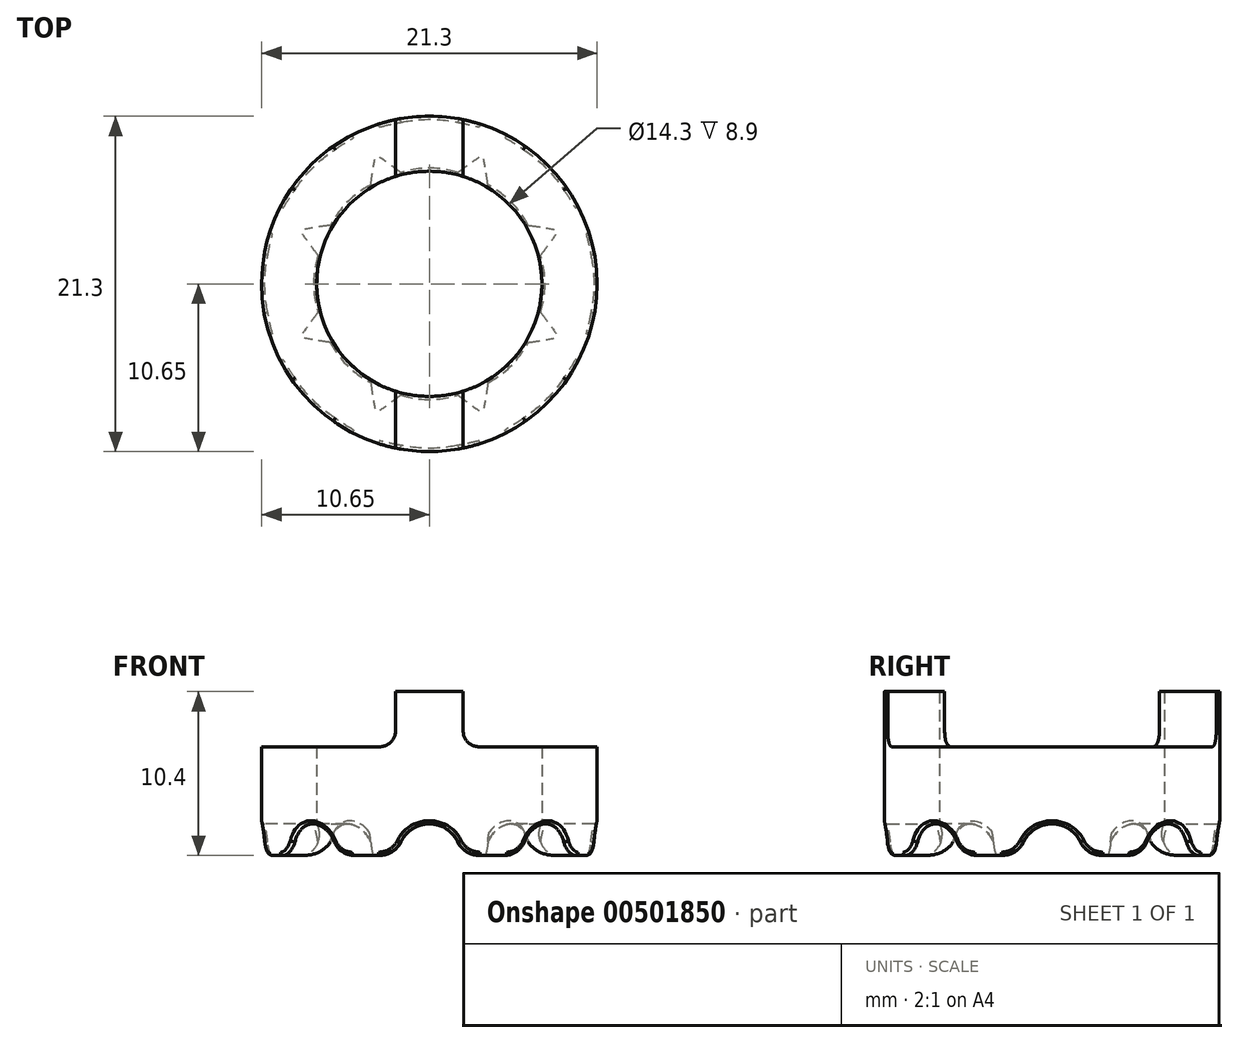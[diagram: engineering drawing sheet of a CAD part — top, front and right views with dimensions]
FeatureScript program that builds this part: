
annotation { "Feature Type Name" : "Feature", "Feature Type Description" : "" }
export const myFeature = defineFeature(function(context is Context, id is Id, definition is map)
    precondition{}
    {
        {
            var Q0;
            Q0=qCreatedBy(makeId("Top.planeOp"),FACE);
            var sketch = newSketch(context, id + "F0", { "sketchPlane" : qUnion([Q0])});
            skCircle(sketch, "E0", {"center": v(0, 0) * mm, "radius": 7.15 * mm});
            skCircle(sketch, "E1", {"center": v(0, 0) * mm, "radius": 10.65 * mm});
            skSolve(sketch);
        }
        {
            var Q0;
            Q0 = qSketchRegion(id + "F0", true);
            extrude(context, id + "F1", {"entities" : qUnion([Q0]), "depth" : 10.4 * mm});
        }
        {
            var Q0;
            Q0=qCreatedBy(makeId("Front.planeOp"),FACE);
            var sketch = newSketch(context, id + "F2", { "sketchPlane" : qUnion([Q0])});
            skLineSegment(sketch, "E2.0", {"start": v(-10.65, 10.4) * mm, "end": v(-2.15, 10.4) * mm});
            skLineSegment(sketch, "E3.0", {"start": v(-10.65, 6.9) * mm, "end": v(-3.15, 6.9) * mm});
            skLineSegment(sketch, "E4.0", {"start": v(-2.15, 10.4) * mm, "end": v(-2.15, 7.9) * mm});
            skLineSegment(sketch, "E5.0", {"start": v(2.15, 10.4) * mm, "end": v(2.15, 7.9) * mm});
            skLineSegment(sketch, "E6", {"start": v(-10.65, 10.4) * mm, "end": v(-10.65, 6.9) * mm});
            skLineSegment(sketch, "E7", {"start": v(10.65, 10.4) * mm, "end": v(10.65, 6.9) * mm});
            skLineSegment(sketch, "E8.trimOffspring", {"start": v(3.15, 6.9) * mm, "end": v(10.65, 6.9) * mm});
            skLineSegment(sketch, "E9.trimOffspring", {"start": v(2.15, 10.4) * mm, "end": v(10.65, 10.4) * mm});
            skPoint(sketch, "E10.visualSharp", {"position": v(-2.15, 6.9) * mm});
            skArc(sketch, "E10.filletArc", {"start": v(-3.15, 6.9) * mm, "mid": v(-2.44, 7.2) * mm, "end": v(-2.15, 7.9) * mm});
            skPoint(sketch, "E11.visualSharp", {"position": v(2.15, 6.9) * mm});
            skArc(sketch, "E11.filletArc", {"start": v(2.15, 7.9) * mm, "mid": v(2.44, 7.2) * mm, "end": v(3.15, 6.9) * mm});
            skSolve(sketch);
        }
        {
            var Q0;
            Q0 = qSketchRegion(id + "F2", true);
            extrude(context, id + "F3", {"entities" : qUnion([Q0]), "operationType" : NewBodyOperationType.REMOVE, "endBound" : BoundingType.THROUGH_ALL, "oppositeDirection" : true, "depth" : 25 * mm, "hasSecondDirection" : true, "secondDirectionBound" : SecondDirectionBoundingType.THROUGH_ALL, "secondDirectionOppositeDirection" : false, "secondDirectionDepth" : 25 * mm});
        }
        {
            var Q0;
            Q0=qCreatedBy(makeId("Front.planeOp"),FACE);
            var sketch = newSketch(context, id + "F4", { "sketchPlane" : qUnion([Q0])});
            skCircle(sketch, "E12", {"center": v(0, 0) * mm, "radius": 2 * mm});
            skSolve(sketch);
        }
        {
            var Q0;
            Q0 = qSketchRegion(id + "F4", true);
            extrude(context, id + "F5", {"entities" : qUnion([Q0]), "operationType" : NewBodyOperationType.REMOVE, "endBound" : BoundingType.THROUGH_ALL, "depth" : 25 * mm, "hasSecondDirection" : true, "secondDirectionBound" : SecondDirectionBoundingType.THROUGH_ALL, "secondDirectionOppositeDirection" : true, "secondDirectionDepth" : 25 * mm});
        }
        {
            var Q0;
            Q0=qCreatedBy(makeId("Right.planeOp"),FACE);
            var sketch = newSketch(context, id + "F6", { "sketchPlane" : qUnion([Q0])});
            skCircle(sketch, "E13", {"center": v(0, 0) * mm, "radius": 2 * mm});
            skSolve(sketch);
        }
        {
            var Q0;
            Q0 = qSketchRegion(id + "F6", true);
            extrude(context, id + "F7", {"entities" : qUnion([Q0]), "operationType" : NewBodyOperationType.REMOVE, "endBound" : BoundingType.THROUGH_ALL, "depth" : 25 * mm, "hasSecondDirection" : true, "secondDirectionBound" : SecondDirectionBoundingType.THROUGH_ALL, "secondDirectionOppositeDirection" : true, "secondDirectionDepth" : 25 * mm});
        }
        {
            var Q0;
            Q0=qCreatedBy(makeId("Front.planeOp"),FACE);
            var sketch = newSketch(context, id + "F8", { "sketchPlane" : qUnion([Q0])});
            skLineSegment(sketch, "E14", {"start": v(0, 0) * mm, "end": v(0, -32.86) * mm});
            skLineSegment(sketch, "E15", {"start": v(0, 0) * mm, "end": v(12.09, 0) * mm});
            skSolve(sketch);
        }
        {
            var Q0;
            Q0=sQuery(id+"F8.wireOp",EDGE,"E14");
            cPlane(context, id + "F9", {"entities" : qUnion([Q0]), "cplaneType" : CPlaneType.LINE_ANGLE, "offset" : 25 * mm, "angle" : 45 * degree, "width" : 150 * mm, "height" : 150 * mm});
        }
        {
            var Q0;
            Q0=sQuery(id+"F8.wireOp",EDGE,"E14");
            cPlane(context, id + "F10", {"entities" : qUnion([Q0]), "cplaneType" : CPlaneType.LINE_ANGLE, "offset" : 25 * mm, "angle" : 135 * degree, "width" : 150 * mm, "height" : 150 * mm});
        }
        {
            var Q0;
            Q0=qCreatedBy(id+"F10.planeOp",FACE);
            var sketch = newSketch(context, id + "F11", { "sketchPlane" : qUnion([Q0])});
            skCircle(sketch, "E16", {"center": v(0, 0) * mm, "radius": 2 * mm});
            skSolve(sketch);
        }
        {
            var Q0;
            Q0 = qSketchRegion(id + "F11", true);
            extrude(context, id + "F12", {"entities" : qUnion([Q0]), "operationType" : NewBodyOperationType.REMOVE, "endBound" : BoundingType.THROUGH_ALL, "depth" : 25 * mm, "hasSecondDirection" : true, "secondDirectionBound" : SecondDirectionBoundingType.THROUGH_ALL, "secondDirectionOppositeDirection" : true, "secondDirectionDepth" : 25 * mm});
        }
        {
            var Q0;
            Q0=qCreatedBy(id+"F9.planeOp",FACE);
            var sketch = newSketch(context, id + "F13", { "sketchPlane" : qUnion([Q0])});
            skCircle(sketch, "E17", {"center": v(0, 0) * mm, "radius": 2 * mm});
            skSolve(sketch);
        }
        {
            var Q0;
            Q0 = qSketchRegion(id + "F13", true);
            extrude(context, id + "F14", {"entities" : qUnion([Q0]), "operationType" : NewBodyOperationType.REMOVE, "endBound" : BoundingType.THROUGH_ALL, "depth" : 25 * mm, "hasSecondDirection" : true, "secondDirectionBound" : SecondDirectionBoundingType.THROUGH_ALL, "secondDirectionOppositeDirection" : true, "secondDirectionDepth" : 25 * mm});
        }
        {
            var Q0;
            {var subQ0=sQuery(id+"F0.wireOp",EDGE,"E0");var subQ1=sQuery(id+"F0.wireOp",EDGE,"E1");Q0=makeQuery(id+"F14.boolean.opBoolean","INTERSECT",EDGE,{"disambiguationData":[OD(1.0)],"derivedFrom":[makeQuery(id+"F7.boolean.opBoolean","SPLIT",FACE,{"disambiguationData":[TD([makeQuery(id+"F5.boolean.opBoolean","COPY",FACE,{"disambiguationData":[OD(0.0)],"derivedFrom":makeQuery(id+"F5.opExtrude","SWEPT_FACE",FACE,{"disambiguationData":[OSD([sQuery(id+"F4.wireOp",EDGE,"E12")])]})})])],"derivedFrom":makeQuery(id+"F5.boolean.opBoolean","SPLIT",FACE,{"disambiguationData":[OD(1.0)],"derivedFrom":makeQuery(id+"F1.opExtrude","CAP_FACE",FACE,{"disambiguationData":[OSD([subQ0,subQ1])],"isStart":true})})}),makeQuery(id+"F14.opExtrude","SWEPT_FACE",FACE,{"disambiguationData":[OSD([sQuery(id+"F13.wireOp",EDGE,"E17")])]})]});}
            var Q1;
            Q1=makeQuery(id+"F7.boolean.opBoolean","INTERSECT",EDGE,{"disambiguationData":[OD(0.0)],"derivedFrom":[makeQuery(id+"F5.boolean.opBoolean","SPLIT",FACE,{"disambiguationData":[OD(1.0)],"derivedFrom":makeQuery(id+"F1.opExtrude","CAP_FACE",FACE,{"disambiguationData":[OSD([sQuery(id+"F0.wireOp",EDGE,"E0"),sQuery(id+"F0.wireOp",EDGE,"E1")])],"isStart":true})}),makeQuery(id+"F7.opExtrude","SWEPT_FACE",FACE,{"disambiguationData":[OSD([sQuery(id+"F6.wireOp",EDGE,"E13")])]})]});
            var Q2;
            {var subQ0=sQuery(id+"F0.wireOp",EDGE,"E0");var subQ3=makeQuery(id+"F7.opExtrude","SWEPT_FACE",FACE,{"disambiguationData":[OSD([sQuery(id+"F6.wireOp",EDGE,"E13")])]});Q2=makeQuery(id+"F14.boolean.opBoolean","SPLIT",EDGE,{"disambiguationData":[TD([makeQuery(id+"F7.boolean.opBoolean","COPY",FACE,{"disambiguationData":[OD(1.0)],"derivedFrom":subQ3})])],"derivedFrom":makeQuery(id+"F7.boolean.opBoolean","SPLIT",EDGE,{"disambiguationData":[TD([makeQuery(id+"F5.boolean.opBoolean","COPY",FACE,{"disambiguationData":[OD(0.0)],"derivedFrom":makeQuery(id+"F5.opExtrude","SWEPT_FACE",FACE,{"disambiguationData":[OSD([sQuery(id+"F4.wireOp",EDGE,"E12")])]})})])],"derivedFrom":makeQuery(id+"F5.boolean.opBoolean","SPLIT",EDGE,{"disambiguationData":[OD(1.0)],"derivedFrom":makeQuery(id+"F1.opExtrude","CAP_EDGE",EDGE,{"disambiguationData":[OSD([subQ0])],"isStart":true})})})});}
            var Q3;
            {var subQ0=sQuery(id+"F0.wireOp",EDGE,"E0");var subQ3=makeQuery(id+"F5.boolean.opBoolean","COPY",FACE,{"disambiguationData":[OD(0.0)],"derivedFrom":makeQuery(id+"F5.opExtrude","SWEPT_FACE",FACE,{"disambiguationData":[OSD([sQuery(id+"F4.wireOp",EDGE,"E12")])]})});Q3=makeQuery(id+"F14.boolean.opBoolean","SPLIT",EDGE,{"disambiguationData":[TD([subQ3])],"derivedFrom":makeQuery(id+"F7.boolean.opBoolean","SPLIT",EDGE,{"disambiguationData":[TD([subQ3])],"derivedFrom":makeQuery(id+"F5.boolean.opBoolean","SPLIT",EDGE,{"disambiguationData":[OD(1.0)],"derivedFrom":makeQuery(id+"F1.opExtrude","CAP_EDGE",EDGE,{"disambiguationData":[OSD([subQ0])],"isStart":true})})})});}
            var Q4;
            {var subQ0=sQuery(id+"F0.wireOp",EDGE,"E0");var subQ3=makeQuery(id+"F5.boolean.opBoolean","COPY",FACE,{"disambiguationData":[OD(0.0)],"derivedFrom":makeQuery(id+"F5.opExtrude","SWEPT_FACE",FACE,{"disambiguationData":[OSD([sQuery(id+"F4.wireOp",EDGE,"E12")])]})});Q4=makeQuery(id+"F12.boolean.opBoolean","SPLIT",EDGE,{"disambiguationData":[TD([subQ3])],"derivedFrom":makeQuery(id+"F7.boolean.opBoolean","SPLIT",EDGE,{"disambiguationData":[TD([subQ3])],"derivedFrom":makeQuery(id+"F5.boolean.opBoolean","SPLIT",EDGE,{"disambiguationData":[OD(0.0)],"derivedFrom":makeQuery(id+"F1.opExtrude","CAP_EDGE",EDGE,{"disambiguationData":[OSD([subQ0])],"isStart":true})})})});}
            var Q5;
            {var subQ0=sQuery(id+"F0.wireOp",EDGE,"E0");var subQ3=makeQuery(id+"F7.opExtrude","SWEPT_FACE",FACE,{"disambiguationData":[OSD([sQuery(id+"F6.wireOp",EDGE,"E13")])]});Q5=makeQuery(id+"F12.boolean.opBoolean","SPLIT",EDGE,{"disambiguationData":[TD([makeQuery(id+"F7.boolean.opBoolean","COPY",FACE,{"disambiguationData":[OD(0.0)],"derivedFrom":subQ3})])],"derivedFrom":makeQuery(id+"F7.boolean.opBoolean","SPLIT",EDGE,{"disambiguationData":[TD([makeQuery(id+"F5.boolean.opBoolean","COPY",FACE,{"disambiguationData":[OD(0.0)],"derivedFrom":makeQuery(id+"F5.opExtrude","SWEPT_FACE",FACE,{"disambiguationData":[OSD([sQuery(id+"F4.wireOp",EDGE,"E12")])]})})])],"derivedFrom":makeQuery(id+"F5.boolean.opBoolean","SPLIT",EDGE,{"disambiguationData":[OD(0.0)],"derivedFrom":makeQuery(id+"F1.opExtrude","CAP_EDGE",EDGE,{"disambiguationData":[OSD([subQ0])],"isStart":true})})})});}
            var Q6;
            {var subQ0=sQuery(id+"F0.wireOp",EDGE,"E0");var subQ3=makeQuery(id+"F7.opExtrude","SWEPT_FACE",FACE,{"disambiguationData":[OSD([sQuery(id+"F6.wireOp",EDGE,"E13")])]});Q6=makeQuery(id+"F14.boolean.opBoolean","SPLIT",EDGE,{"disambiguationData":[TD([makeQuery(id+"F7.boolean.opBoolean","COPY",FACE,{"disambiguationData":[OD(0.0)],"derivedFrom":subQ3})])],"derivedFrom":makeQuery(id+"F7.boolean.opBoolean","SPLIT",EDGE,{"disambiguationData":[TD([makeQuery(id+"F5.boolean.opBoolean","COPY",FACE,{"disambiguationData":[OD(1.0)],"derivedFrom":makeQuery(id+"F5.opExtrude","SWEPT_FACE",FACE,{"disambiguationData":[OSD([sQuery(id+"F4.wireOp",EDGE,"E12")])]})})])],"derivedFrom":makeQuery(id+"F5.boolean.opBoolean","SPLIT",EDGE,{"disambiguationData":[OD(0.0)],"derivedFrom":makeQuery(id+"F1.opExtrude","CAP_EDGE",EDGE,{"disambiguationData":[OSD([subQ0])],"isStart":true})})})});}
            var Q7;
            {var subQ0=sQuery(id+"F0.wireOp",EDGE,"E0");var subQ3=makeQuery(id+"F5.boolean.opBoolean","COPY",FACE,{"disambiguationData":[OD(1.0)],"derivedFrom":makeQuery(id+"F5.opExtrude","SWEPT_FACE",FACE,{"disambiguationData":[OSD([sQuery(id+"F4.wireOp",EDGE,"E12")])]})});Q7=makeQuery(id+"F14.boolean.opBoolean","SPLIT",EDGE,{"disambiguationData":[TD([subQ3])],"derivedFrom":makeQuery(id+"F7.boolean.opBoolean","SPLIT",EDGE,{"disambiguationData":[TD([subQ3])],"derivedFrom":makeQuery(id+"F5.boolean.opBoolean","SPLIT",EDGE,{"disambiguationData":[OD(0.0)],"derivedFrom":makeQuery(id+"F1.opExtrude","CAP_EDGE",EDGE,{"disambiguationData":[OSD([subQ0])],"isStart":true})})})});}
            var Q8;
            {var subQ0=sQuery(id+"F0.wireOp",EDGE,"E0");var subQ3=makeQuery(id+"F5.boolean.opBoolean","COPY",FACE,{"disambiguationData":[OD(1.0)],"derivedFrom":makeQuery(id+"F5.opExtrude","SWEPT_FACE",FACE,{"disambiguationData":[OSD([sQuery(id+"F4.wireOp",EDGE,"E12")])]})});Q8=makeQuery(id+"F12.boolean.opBoolean","SPLIT",EDGE,{"disambiguationData":[TD([subQ3])],"derivedFrom":makeQuery(id+"F7.boolean.opBoolean","SPLIT",EDGE,{"disambiguationData":[TD([subQ3])],"derivedFrom":makeQuery(id+"F5.boolean.opBoolean","SPLIT",EDGE,{"disambiguationData":[OD(1.0)],"derivedFrom":makeQuery(id+"F1.opExtrude","CAP_EDGE",EDGE,{"disambiguationData":[OSD([subQ0])],"isStart":true})})})});}
            var Q9;
            {var subQ0=sQuery(id+"F0.wireOp",EDGE,"E0");var subQ3=makeQuery(id+"F7.opExtrude","SWEPT_FACE",FACE,{"disambiguationData":[OSD([sQuery(id+"F6.wireOp",EDGE,"E13")])]});Q9=makeQuery(id+"F12.boolean.opBoolean","SPLIT",EDGE,{"disambiguationData":[TD([makeQuery(id+"F7.boolean.opBoolean","COPY",FACE,{"disambiguationData":[OD(1.0)],"derivedFrom":subQ3})])],"derivedFrom":makeQuery(id+"F7.boolean.opBoolean","SPLIT",EDGE,{"disambiguationData":[TD([makeQuery(id+"F5.boolean.opBoolean","COPY",FACE,{"disambiguationData":[OD(1.0)],"derivedFrom":makeQuery(id+"F5.opExtrude","SWEPT_FACE",FACE,{"disambiguationData":[OSD([sQuery(id+"F4.wireOp",EDGE,"E12")])]})})])],"derivedFrom":makeQuery(id+"F5.boolean.opBoolean","SPLIT",EDGE,{"disambiguationData":[OD(1.0)],"derivedFrom":makeQuery(id+"F1.opExtrude","CAP_EDGE",EDGE,{"disambiguationData":[OSD([subQ0])],"isStart":true})})})});}
            var Q10;
            Q10=makeQuery(id+"F7.boolean.opBoolean","INTERSECT",EDGE,{"disambiguationData":[OD(1.0)],"derivedFrom":[makeQuery(id+"F5.boolean.opBoolean","SPLIT",FACE,{"disambiguationData":[OD(1.0)],"derivedFrom":makeQuery(id+"F1.opExtrude","CAP_FACE",FACE,{"disambiguationData":[OSD([sQuery(id+"F0.wireOp",EDGE,"E0"),sQuery(id+"F0.wireOp",EDGE,"E1")])],"isStart":true})}),makeQuery(id+"F7.opExtrude","SWEPT_FACE",FACE,{"disambiguationData":[OSD([sQuery(id+"F6.wireOp",EDGE,"E13")])]})]});
            var Q11;
            {var subQ0=sQuery(id+"F0.wireOp",EDGE,"E0");var subQ1=sQuery(id+"F0.wireOp",EDGE,"E1");Q11=makeQuery(id+"F12.boolean.opBoolean","INTERSECT",EDGE,{"disambiguationData":[OD(1.0)],"derivedFrom":[makeQuery(id+"F7.boolean.opBoolean","SPLIT",FACE,{"disambiguationData":[TD([makeQuery(id+"F5.boolean.opBoolean","COPY",FACE,{"disambiguationData":[OD(1.0)],"derivedFrom":makeQuery(id+"F5.opExtrude","SWEPT_FACE",FACE,{"disambiguationData":[OSD([sQuery(id+"F4.wireOp",EDGE,"E12")])]})})])],"derivedFrom":makeQuery(id+"F5.boolean.opBoolean","SPLIT",FACE,{"disambiguationData":[OD(1.0)],"derivedFrom":makeQuery(id+"F1.opExtrude","CAP_FACE",FACE,{"disambiguationData":[OSD([subQ0,subQ1])],"isStart":true})})}),makeQuery(id+"F12.opExtrude","SWEPT_FACE",FACE,{"disambiguationData":[OSD([sQuery(id+"F11.wireOp",EDGE,"E16")])]})]});}
            var Q12;
            {var subQ0=sQuery(id+"F0.wireOp",EDGE,"E0");var subQ1=sQuery(id+"F0.wireOp",EDGE,"E1");Q12=makeQuery(id+"F12.boolean.opBoolean","INTERSECT",EDGE,{"disambiguationData":[OD(0.0)],"derivedFrom":[makeQuery(id+"F7.boolean.opBoolean","SPLIT",FACE,{"disambiguationData":[TD([makeQuery(id+"F5.boolean.opBoolean","COPY",FACE,{"disambiguationData":[OD(1.0)],"derivedFrom":makeQuery(id+"F5.opExtrude","SWEPT_FACE",FACE,{"disambiguationData":[OSD([sQuery(id+"F4.wireOp",EDGE,"E12")])]})})])],"derivedFrom":makeQuery(id+"F5.boolean.opBoolean","SPLIT",FACE,{"disambiguationData":[OD(1.0)],"derivedFrom":makeQuery(id+"F1.opExtrude","CAP_FACE",FACE,{"disambiguationData":[OSD([subQ0,subQ1])],"isStart":true})})}),makeQuery(id+"F12.opExtrude","SWEPT_FACE",FACE,{"disambiguationData":[OSD([sQuery(id+"F11.wireOp",EDGE,"E16")])]})]});}
            var Q13;
            Q13=makeQuery(id+"F5.boolean.opBoolean","INTERSECT",EDGE,{"disambiguationData":[OD(3.0)],"derivedFrom":[makeQuery(id+"F1.opExtrude","CAP_FACE",FACE,{"disambiguationData":[OSD([sQuery(id+"F0.wireOp",EDGE,"E0"),sQuery(id+"F0.wireOp",EDGE,"E1")])],"isStart":true}),makeQuery(id+"F5.opExtrude","SWEPT_FACE",FACE,{"disambiguationData":[OSD([sQuery(id+"F4.wireOp",EDGE,"E12")])]})]});
            var Q14;
            Q14=makeQuery(id+"F5.boolean.opBoolean","INTERSECT",EDGE,{"disambiguationData":[OD(2.0)],"derivedFrom":[makeQuery(id+"F1.opExtrude","CAP_FACE",FACE,{"disambiguationData":[OSD([sQuery(id+"F0.wireOp",EDGE,"E0"),sQuery(id+"F0.wireOp",EDGE,"E1")])],"isStart":true}),makeQuery(id+"F5.opExtrude","SWEPT_FACE",FACE,{"disambiguationData":[OSD([sQuery(id+"F4.wireOp",EDGE,"E12")])]})]});
            var Q15;
            {var subQ0=sQuery(id+"F0.wireOp",EDGE,"E0");var subQ1=sQuery(id+"F0.wireOp",EDGE,"E1");Q15=makeQuery(id+"F14.boolean.opBoolean","INTERSECT",EDGE,{"disambiguationData":[OD(0.0)],"derivedFrom":[makeQuery(id+"F7.boolean.opBoolean","SPLIT",FACE,{"disambiguationData":[TD([makeQuery(id+"F5.boolean.opBoolean","COPY",FACE,{"disambiguationData":[OD(1.0)],"derivedFrom":makeQuery(id+"F5.opExtrude","SWEPT_FACE",FACE,{"disambiguationData":[OSD([sQuery(id+"F4.wireOp",EDGE,"E12")])]})})])],"derivedFrom":makeQuery(id+"F5.boolean.opBoolean","SPLIT",FACE,{"disambiguationData":[OD(0.0)],"derivedFrom":makeQuery(id+"F1.opExtrude","CAP_FACE",FACE,{"disambiguationData":[OSD([subQ0,subQ1])],"isStart":true})})}),makeQuery(id+"F14.opExtrude","SWEPT_FACE",FACE,{"disambiguationData":[OSD([sQuery(id+"F13.wireOp",EDGE,"E17")])]})]});}
            var Q16;
            {var subQ0=sQuery(id+"F0.wireOp",EDGE,"E0");var subQ1=sQuery(id+"F0.wireOp",EDGE,"E1");Q16=makeQuery(id+"F14.boolean.opBoolean","INTERSECT",EDGE,{"disambiguationData":[OD(1.0)],"derivedFrom":[makeQuery(id+"F7.boolean.opBoolean","SPLIT",FACE,{"disambiguationData":[TD([makeQuery(id+"F5.boolean.opBoolean","COPY",FACE,{"disambiguationData":[OD(1.0)],"derivedFrom":makeQuery(id+"F5.opExtrude","SWEPT_FACE",FACE,{"disambiguationData":[OSD([sQuery(id+"F4.wireOp",EDGE,"E12")])]})})])],"derivedFrom":makeQuery(id+"F5.boolean.opBoolean","SPLIT",FACE,{"disambiguationData":[OD(0.0)],"derivedFrom":makeQuery(id+"F1.opExtrude","CAP_FACE",FACE,{"disambiguationData":[OSD([subQ0,subQ1])],"isStart":true})})}),makeQuery(id+"F14.opExtrude","SWEPT_FACE",FACE,{"disambiguationData":[OSD([sQuery(id+"F13.wireOp",EDGE,"E17")])]})]});}
            var Q17;
            Q17=makeQuery(id+"F7.boolean.opBoolean","INTERSECT",EDGE,{"disambiguationData":[OD(1.0)],"derivedFrom":[makeQuery(id+"F5.boolean.opBoolean","SPLIT",FACE,{"disambiguationData":[OD(0.0)],"derivedFrom":makeQuery(id+"F1.opExtrude","CAP_FACE",FACE,{"disambiguationData":[OSD([sQuery(id+"F0.wireOp",EDGE,"E0"),sQuery(id+"F0.wireOp",EDGE,"E1")])],"isStart":true})}),makeQuery(id+"F7.opExtrude","SWEPT_FACE",FACE,{"disambiguationData":[OSD([sQuery(id+"F6.wireOp",EDGE,"E13")])]})]});
            var Q18;
            Q18=makeQuery(id+"F7.boolean.opBoolean","INTERSECT",EDGE,{"disambiguationData":[OD(0.0)],"derivedFrom":[makeQuery(id+"F5.boolean.opBoolean","SPLIT",FACE,{"disambiguationData":[OD(0.0)],"derivedFrom":makeQuery(id+"F1.opExtrude","CAP_FACE",FACE,{"disambiguationData":[OSD([sQuery(id+"F0.wireOp",EDGE,"E0"),sQuery(id+"F0.wireOp",EDGE,"E1")])],"isStart":true})}),makeQuery(id+"F7.opExtrude","SWEPT_FACE",FACE,{"disambiguationData":[OSD([sQuery(id+"F6.wireOp",EDGE,"E13")])]})]});
            var Q19;
            {var subQ0=sQuery(id+"F0.wireOp",EDGE,"E0");var subQ1=sQuery(id+"F0.wireOp",EDGE,"E1");Q19=makeQuery(id+"F12.boolean.opBoolean","INTERSECT",EDGE,{"disambiguationData":[OD(1.0)],"derivedFrom":[makeQuery(id+"F7.boolean.opBoolean","SPLIT",FACE,{"disambiguationData":[TD([makeQuery(id+"F5.boolean.opBoolean","COPY",FACE,{"disambiguationData":[OD(0.0)],"derivedFrom":makeQuery(id+"F5.opExtrude","SWEPT_FACE",FACE,{"disambiguationData":[OSD([sQuery(id+"F4.wireOp",EDGE,"E12")])]})})])],"derivedFrom":makeQuery(id+"F5.boolean.opBoolean","SPLIT",FACE,{"disambiguationData":[OD(0.0)],"derivedFrom":makeQuery(id+"F1.opExtrude","CAP_FACE",FACE,{"disambiguationData":[OSD([subQ0,subQ1])],"isStart":true})})}),makeQuery(id+"F12.opExtrude","SWEPT_FACE",FACE,{"disambiguationData":[OSD([sQuery(id+"F11.wireOp",EDGE,"E16")])]})]});}
            var Q20;
            {var subQ0=sQuery(id+"F0.wireOp",EDGE,"E0");var subQ1=sQuery(id+"F0.wireOp",EDGE,"E1");Q20=makeQuery(id+"F12.boolean.opBoolean","INTERSECT",EDGE,{"disambiguationData":[OD(0.0)],"derivedFrom":[makeQuery(id+"F7.boolean.opBoolean","SPLIT",FACE,{"disambiguationData":[TD([makeQuery(id+"F5.boolean.opBoolean","COPY",FACE,{"disambiguationData":[OD(0.0)],"derivedFrom":makeQuery(id+"F5.opExtrude","SWEPT_FACE",FACE,{"disambiguationData":[OSD([sQuery(id+"F4.wireOp",EDGE,"E12")])]})})])],"derivedFrom":makeQuery(id+"F5.boolean.opBoolean","SPLIT",FACE,{"disambiguationData":[OD(0.0)],"derivedFrom":makeQuery(id+"F1.opExtrude","CAP_FACE",FACE,{"disambiguationData":[OSD([subQ0,subQ1])],"isStart":true})})}),makeQuery(id+"F12.opExtrude","SWEPT_FACE",FACE,{"disambiguationData":[OSD([sQuery(id+"F11.wireOp",EDGE,"E16")])]})]});}
            var Q21;
            Q21=makeQuery(id+"F5.boolean.opBoolean","INTERSECT",EDGE,{"disambiguationData":[OD(0.0)],"derivedFrom":[makeQuery(id+"F1.opExtrude","CAP_FACE",FACE,{"disambiguationData":[OSD([sQuery(id+"F0.wireOp",EDGE,"E0"),sQuery(id+"F0.wireOp",EDGE,"E1")])],"isStart":true}),makeQuery(id+"F5.opExtrude","SWEPT_FACE",FACE,{"disambiguationData":[OSD([sQuery(id+"F4.wireOp",EDGE,"E12")])]})]});
            var Q22;
            Q22=makeQuery(id+"F5.boolean.opBoolean","INTERSECT",EDGE,{"disambiguationData":[OD(1.0)],"derivedFrom":[makeQuery(id+"F1.opExtrude","CAP_FACE",FACE,{"disambiguationData":[OSD([sQuery(id+"F0.wireOp",EDGE,"E0"),sQuery(id+"F0.wireOp",EDGE,"E1")])],"isStart":true}),makeQuery(id+"F5.opExtrude","SWEPT_FACE",FACE,{"disambiguationData":[OSD([sQuery(id+"F4.wireOp",EDGE,"E12")])]})]});
            var Q23;
            {var subQ0=sQuery(id+"F0.wireOp",EDGE,"E0");var subQ1=sQuery(id+"F0.wireOp",EDGE,"E1");Q23=makeQuery(id+"F14.boolean.opBoolean","INTERSECT",EDGE,{"disambiguationData":[OD(0.0)],"derivedFrom":[makeQuery(id+"F7.boolean.opBoolean","SPLIT",FACE,{"disambiguationData":[TD([makeQuery(id+"F5.boolean.opBoolean","COPY",FACE,{"disambiguationData":[OD(0.0)],"derivedFrom":makeQuery(id+"F5.opExtrude","SWEPT_FACE",FACE,{"disambiguationData":[OSD([sQuery(id+"F4.wireOp",EDGE,"E12")])]})})])],"derivedFrom":makeQuery(id+"F5.boolean.opBoolean","SPLIT",FACE,{"disambiguationData":[OD(1.0)],"derivedFrom":makeQuery(id+"F1.opExtrude","CAP_FACE",FACE,{"disambiguationData":[OSD([subQ0,subQ1])],"isStart":true})})}),makeQuery(id+"F14.opExtrude","SWEPT_FACE",FACE,{"disambiguationData":[OSD([sQuery(id+"F13.wireOp",EDGE,"E17")])]})]});}
            fillet(context, id + "F15", {"entities" : qUnion([Q0, Q1, Q2, Q3, Q4, Q5, Q6, Q7, Q8, Q9, Q10, Q11, Q12, Q13, Q14, Q15, Q16, Q17, Q18, Q19, Q20, Q21, Q22, Q23]), "radius" : 1.5 * mm, "tangentPropagation" : true, "allowEdgeOverflow" : false});
        }
        {
            var Q0;
            Q0=makeQuery(id+"F5.boolean.opBoolean","INTERSECT",EDGE,{"disambiguationData":[OD(1.0)],"derivedFrom":[makeQuery(id+"F1.opExtrude","SWEPT_FACE",FACE,{"disambiguationData":[OSD([sQuery(id+"F0.wireOp",EDGE,"E1")])]}),makeQuery(id+"F5.opExtrude","SWEPT_FACE",FACE,{"disambiguationData":[OSD([sQuery(id+"F4.wireOp",EDGE,"E12")])]})]});
            fillet(context, id + "F16", {"entities" : qUnion([Q0]), "radius" : 0.2 * mm, "tangentPropagation" : true, "allowEdgeOverflow" : false});
        }
        {
            var Q0;
            Q0=makeQuery(id+"F12.boolean.opBoolean","INTERSECT",EDGE,{"disambiguationData":[OD(0.0)],"derivedFrom":[makeQuery(id+"F1.opExtrude","SWEPT_FACE",FACE,{"disambiguationData":[OSD([sQuery(id+"F0.wireOp",EDGE,"E0")])]}),makeQuery(id+"F12.opExtrude","SWEPT_FACE",FACE,{"disambiguationData":[OSD([sQuery(id+"F11.wireOp",EDGE,"E16")])]})]});
            var Q1;
            Q1=makeQuery(id+"F5.boolean.opBoolean","INTERSECT",EDGE,{"disambiguationData":[OD(0.0)],"derivedFrom":[makeQuery(id+"F1.opExtrude","SWEPT_FACE",FACE,{"disambiguationData":[OSD([sQuery(id+"F0.wireOp",EDGE,"E0")])]}),makeQuery(id+"F5.opExtrude","SWEPT_FACE",FACE,{"disambiguationData":[OSD([sQuery(id+"F4.wireOp",EDGE,"E12")])]})]});
            var Q2;
            Q2=makeQuery(id+"F14.boolean.opBoolean","INTERSECT",EDGE,{"disambiguationData":[OD(1.0)],"derivedFrom":[makeQuery(id+"F1.opExtrude","SWEPT_FACE",FACE,{"disambiguationData":[OSD([sQuery(id+"F0.wireOp",EDGE,"E0")])]}),makeQuery(id+"F14.opExtrude","SWEPT_FACE",FACE,{"disambiguationData":[OSD([sQuery(id+"F13.wireOp",EDGE,"E17")])]})]});
            var Q3;
            Q3=makeQuery(id+"F7.boolean.opBoolean","INTERSECT",EDGE,{"disambiguationData":[OD(1.0)],"derivedFrom":[makeQuery(id+"F1.opExtrude","SWEPT_FACE",FACE,{"disambiguationData":[OSD([sQuery(id+"F0.wireOp",EDGE,"E0")])]}),makeQuery(id+"F7.opExtrude","SWEPT_FACE",FACE,{"disambiguationData":[OSD([sQuery(id+"F6.wireOp",EDGE,"E13")])]})]});
            var Q4;
            Q4=makeQuery(id+"F12.boolean.opBoolean","INTERSECT",EDGE,{"disambiguationData":[OD(1.0)],"derivedFrom":[makeQuery(id+"F1.opExtrude","SWEPT_FACE",FACE,{"disambiguationData":[OSD([sQuery(id+"F0.wireOp",EDGE,"E0")])]}),makeQuery(id+"F12.opExtrude","SWEPT_FACE",FACE,{"disambiguationData":[OSD([sQuery(id+"F11.wireOp",EDGE,"E16")])]})]});
            var Q5;
            Q5=makeQuery(id+"F5.boolean.opBoolean","INTERSECT",EDGE,{"disambiguationData":[OD(1.0)],"derivedFrom":[makeQuery(id+"F1.opExtrude","SWEPT_FACE",FACE,{"disambiguationData":[OSD([sQuery(id+"F0.wireOp",EDGE,"E0")])]}),makeQuery(id+"F5.opExtrude","SWEPT_FACE",FACE,{"disambiguationData":[OSD([sQuery(id+"F4.wireOp",EDGE,"E12")])]})]});
            var Q6;
            Q6=makeQuery(id+"F14.boolean.opBoolean","INTERSECT",EDGE,{"disambiguationData":[OD(0.0)],"derivedFrom":[makeQuery(id+"F1.opExtrude","SWEPT_FACE",FACE,{"disambiguationData":[OSD([sQuery(id+"F0.wireOp",EDGE,"E0")])]}),makeQuery(id+"F14.opExtrude","SWEPT_FACE",FACE,{"disambiguationData":[OSD([sQuery(id+"F13.wireOp",EDGE,"E17")])]})]});
            var Q7;
            Q7=makeQuery(id+"F7.boolean.opBoolean","INTERSECT",EDGE,{"disambiguationData":[OD(0.0)],"derivedFrom":[makeQuery(id+"F1.opExtrude","SWEPT_FACE",FACE,{"disambiguationData":[OSD([sQuery(id+"F0.wireOp",EDGE,"E0")])]}),makeQuery(id+"F7.opExtrude","SWEPT_FACE",FACE,{"disambiguationData":[OSD([sQuery(id+"F6.wireOp",EDGE,"E13")])]})]});
            fillet(context, id + "F17", {"entities" : qUnion([Q0, Q1, Q2, Q3, Q4, Q5, Q6, Q7]), "radius" : 0.2 * mm, "allowEdgeOverflow" : false});
        }
    });
